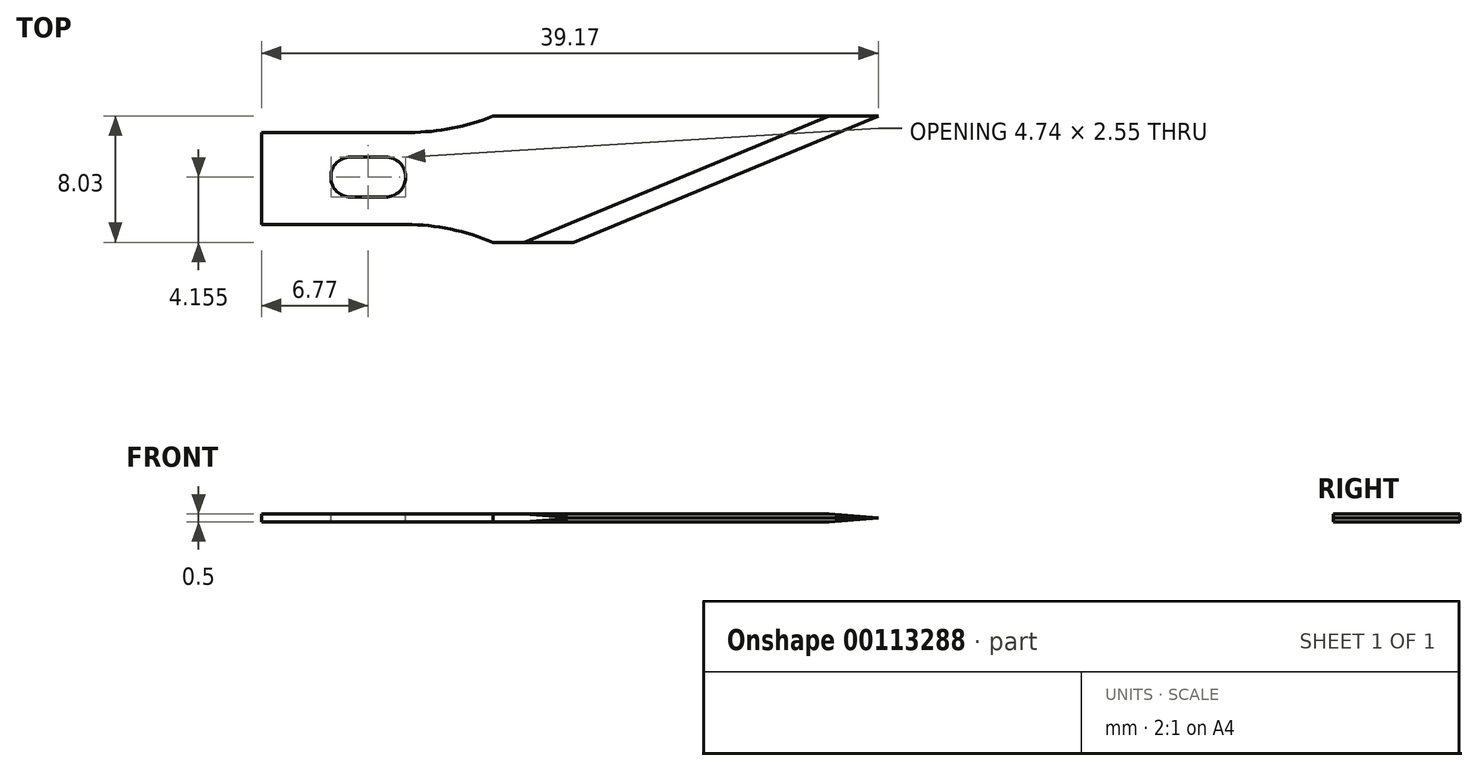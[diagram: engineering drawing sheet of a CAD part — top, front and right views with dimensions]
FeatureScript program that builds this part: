
annotation { "Feature Type Name" : "Feature", "Feature Type Description" : "" }
export const myFeature = defineFeature(function(context is Context, id is Id, definition is map)
    precondition{}
    {
        {
            var Q0;
            Q0=qCreatedBy(makeId("Top.planeOp"),FACE);
            var sketch = newSketch(context, id + "F0", { "sketchPlane" : qUnion([Q0])});
            skLineSegment(sketch, "E0", {"start": v(0, 0) * mm, "end": v(0, 5.86) * mm});
            skLineSegment(sketch, "E1", {"start": v(0, 5.86) * mm, "end": v(14.7, 5.86) * mm});
            skLineSegment(sketch, "E2", {"start": v(14.7, 5.86) * mm, "end": v(14.7, 6.9) * mm});
            skLineSegment(sketch, "E3", {"start": v(14.7, 6.9) * mm, "end": v(39.17, 6.9) * mm});
            skLineSegment(sketch, "E4", {"start": v(39.17, 6.9) * mm, "end": v(19.8, -1.13) * mm});
            skLineSegment(sketch, "E5", {"start": v(19.8, -1.13) * mm, "end": v(14.7, -1.13) * mm});
            skLineSegment(sketch, "E6", {"start": v(14.7, -1.13) * mm, "end": v(14.7, 0) * mm});
            skLineSegment(sketch, "E7", {"start": v(14.7, 0) * mm, "end": v(0, 0) * mm});
            skSolve(sketch);
        }
        {
            var Q0;
            Q0=makeQuery(id+"F0.imprint","IMPRINT",FACE,{"disambiguationData":[TD([[makeQuery(id+"F0.imprint","IMPRINT",EDGE,{"derivedFrom":sQuery(id+"F0.wireOp",EDGE,"E0")}),-1.0]])]});
            extrude(context, id + "F1", {"entities" : qUnion([Q0]), "depth" : 0.5 * mm});
        }
        {
            var Q0;
            Q0=makeQuery(id+"F1.opExtrude","SWEPT_EDGE",EDGE,{"disambiguationData":[OSD([sQuery(id+"F0.wireOp",EDGE,"E1"),sQuery(id+"F0.wireOp",EDGE,"E2")])]});
            var Q1;
            Q1=makeQuery(id+"F1.opExtrude","SWEPT_EDGE",EDGE,{"disambiguationData":[OSD([sQuery(id+"F0.wireOp",EDGE,"E6"),sQuery(id+"F0.wireOp",EDGE,"E7")])]});
            fillet(context, id + "F2", {"entities" : qUnion([Q0, Q1]), "radius" : 14 * mm, "tangentPropagation" : true, "allowEdgeOverflow" : false});
        }
        {
            var Q0;
            Q0=makeQuery(id+"F1.opExtrude","CAP_FACE",FACE,{"disambiguationData":[OSD([sQuery(id+"F0.wireOp",EDGE,"E0"),sQuery(id+"F0.wireOp",EDGE,"E1"),sQuery(id+"F0.wireOp",EDGE,"E2"),sQuery(id+"F0.wireOp",EDGE,"E3"),sQuery(id+"F0.wireOp",EDGE,"E4"),sQuery(id+"F0.wireOp",EDGE,"E5"),sQuery(id+"F0.wireOp",EDGE,"E6"),sQuery(id+"F0.wireOp",EDGE,"E7")])],"isStart":false});
            var sketch = newSketch(context, id + "F3", { "sketchPlane" : qUnion([Q0])});
            skLineSegment(sketch, "E8.bottom", {"start": v(4.4, 4.3) * mm, "end": v(9.14, 4.3) * mm});
            skLineSegment(sketch, "E8.top", {"start": v(4.4, 1.75) * mm, "end": v(9.14, 1.75) * mm});
            skLineSegment(sketch, "E8.left", {"start": v(4.4, 4.3) * mm, "end": v(4.4, 1.75) * mm});
            skLineSegment(sketch, "E8.right", {"start": v(9.14, 4.3) * mm, "end": v(9.14, 1.75) * mm});
            skSolve(sketch);
        }
        {
            var Q0;
            Q0 = qSketchRegion(id + "F3", true);
            extrude(context, id + "F4", {"entities" : qUnion([Q0]), "operationType" : NewBodyOperationType.REMOVE, "endBound" : BoundingType.THROUGH_ALL, "oppositeDirection" : true, "depth" : 25 * mm});
        }
        {
            var Q0;
            Q0=makeQuery(id+"F4.boolean.opBoolean","COPY",EDGE,{"derivedFrom":makeQuery(id+"F4.opExtrude","SWEPT_EDGE",EDGE,{"disambiguationData":[OSD([sQuery(id+"F3.wireOp",EDGE,"E8.top"),sQuery(id+"F3.wireOp",EDGE,"E8.right")])]})});
            var Q1;
            Q1=makeQuery(id+"F4.boolean.opBoolean","COPY",EDGE,{"derivedFrom":makeQuery(id+"F4.opExtrude","SWEPT_EDGE",EDGE,{"disambiguationData":[OSD([sQuery(id+"F3.wireOp",EDGE,"E8.top"),sQuery(id+"F3.wireOp",EDGE,"E8.left")])]})});
            var Q2;
            Q2=makeQuery(id+"F4.boolean.opBoolean","COPY",EDGE,{"derivedFrom":makeQuery(id+"F4.opExtrude","SWEPT_EDGE",EDGE,{"disambiguationData":[OSD([sQuery(id+"F3.wireOp",EDGE,"E8.bottom"),sQuery(id+"F3.wireOp",EDGE,"E8.left")])]})});
            var Q3;
            Q3=makeQuery(id+"F4.boolean.opBoolean","COPY",EDGE,{"derivedFrom":makeQuery(id+"F4.opExtrude","SWEPT_EDGE",EDGE,{"disambiguationData":[OSD([sQuery(id+"F3.wireOp",EDGE,"E8.bottom"),sQuery(id+"F3.wireOp",EDGE,"E8.right")])]})});
            fillet(context, id + "F5", {"entities" : qUnion([Q0, Q1, Q2, Q3]), "radius" : 1.25 * mm, "tangentPropagation" : true, "allowEdgeOverflow" : false});
        }
        {
            var Q0;
            Q0=makeQuery(id+"F1.opExtrude","CAP_EDGE",EDGE,{"disambiguationData":[OSD([sQuery(id+"F0.wireOp",EDGE,"E4")])],"isStart":false});
            var Q1;
            Q1=makeQuery(id+"F1.opExtrude","CAP_EDGE",EDGE,{"disambiguationData":[OSD([sQuery(id+"F0.wireOp",EDGE,"E4")])],"isStart":true});
            chamfer(context, id + "F6", {"entities" : qUnion([Q0, Q1]), "chamferType" : ChamferType.TWO_OFFSETS, "width1" : .25 * mm, "oppositeDirection" : false, "width2" : 1.2 * mm, "tangentPropagation" : true});
        }
    });
